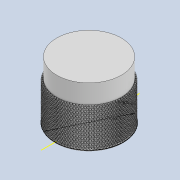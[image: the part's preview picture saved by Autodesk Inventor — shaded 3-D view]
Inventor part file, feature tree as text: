
AUTODESK INVENTOR PART (.ipt)
format: ipt  version: 2021 (Build 250183000, 183)  size: 12,338,176 bytes
history: native  units: mm
features: extrude x3, sketch x2, helix x2, pattern_circular x2, fillet x1
ambient origin geometry x8: Origin, YZ Plane, XZ Plane, XY Plane, X Axis, Y Axis, Z Axis, Center Point
bodies: Solid1 (feature_tree)
feature tree (10):
  sketch  "Sketch1"  dims[d0=18.0mm d1=15.0mm d2=0.0mm]
  extrude  "Extrusion1"  Depth=15.0mm
  helix  "Coil1"  [1 undecoded]
  pattern_circular  "Circular Pattern1"  [2 undecoded]
  helix  "Coil2"  [1 undecoded]
  pattern_circular  "Circular Pattern2"  [2 undecoded]
  extrude  "Extrusion2"  TaperAngle=360.0deg  [1 undecoded]
  extrude  "Extrusion3"  Depth=0.5mm
  fillet  "Fillet1"  Radius=1.25mm
  sketch  "Sketch2"  dims[d3=0.698132mm d4=0.5mm d5=10.0mm d6=10.0mm d7=1.25mm d8=0.0mm d9=90.0deg d10=90.0deg d11=0.0mm d12=0.0mm d13=900.0mm d14=360.0deg d16=10.0mm d17=10.0mm d18=1.25mm d19=0.0mm d20=90.0deg d21=90.0deg d22=0.0mm d23=0.0mm d24=900.0mm d25=360.0deg d27=17.0mm d28=5.0mm d29=0.0mm d30=0.5mm d31=0.0mm d32=0.5mm]
note: 7 required parameter values undecoded (feature->parameter linkage not recoverable at this tier; creation-order binding heuristic only, values carry confidence <= 0.55)
